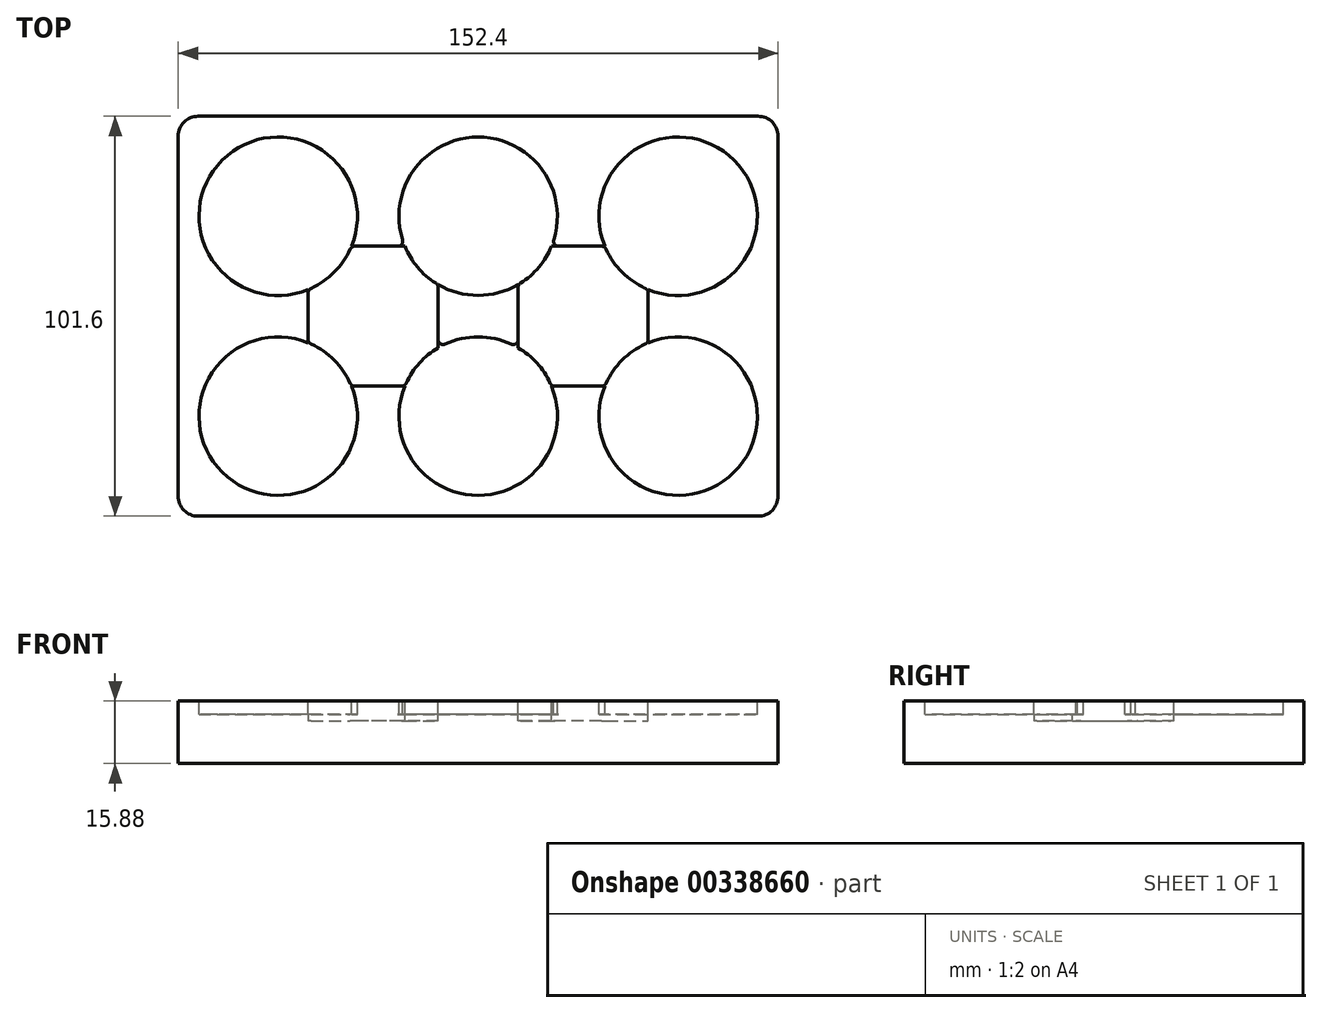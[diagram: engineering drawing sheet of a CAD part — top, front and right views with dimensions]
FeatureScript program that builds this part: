
annotation { "Feature Type Name" : "Feature", "Feature Type Description" : "" }
export const myFeature = defineFeature(function(context is Context, id is Id, definition is map)
    precondition{}
    {
        {
            var Q0;
            Q0=qCreatedBy(makeId("Top.planeOp"),FACE);
            var sketch = newSketch(context, id + "F0", { "sketchPlane" : qUnion([Q0])});
            skLineSegment(sketch, "E0.bottom", {"start": v(0, 0) * mm, "end": v(33.02, 0) * mm});
            skLineSegment(sketch, "E0.top", {"start": v(0, 101.6) * mm, "end": v(25.4, 101.6) * mm});
            skLineSegment(sketch, "E0.left", {"start": v(0, 0) * mm, "end": v(0, 25.4) * mm});
            skLineSegment(sketch, "E0.right", {"start": v(152.4, 0) * mm, "end": v(152.4, 33.02) * mm});
            skCircle(sketch, "E1", {"center": v(25.4, 25.4) * mm, "radius": 20.13 * mm});
            skCircle(sketch, "E2", {"center": v(25.4, 76.2) * mm, "radius": 20.13 * mm});
            skLineSegment(sketch, "E3", {"start": v(0, 76.2) * mm, "end": v(0, 101.6) * mm});
            skLineSegment(sketch, "E4", {"start": v(0, 25.4) * mm, "end": v(0, 76.2) * mm});
            skLineSegment(sketch, "E5", {"start": v(25.4, 101.6) * mm, "end": v(76.2, 101.6) * mm});
            skLineSegment(sketch, "E6", {"start": v(76.2, 101.6) * mm, "end": v(127, 101.6) * mm});
            skLineSegment(sketch, "E7", {"start": v(127, 101.6) * mm, "end": v(152.4, 101.6) * mm});
            skCircle(sketch, "E8", {"center": v(76.2, 76.2) * mm, "radius": 20.13 * mm});
            skCircle(sketch, "E9", {"center": v(76.2, 25.4) * mm, "radius": 20.13 * mm});
            skCircle(sketch, "E10", {"center": v(127, 76.2) * mm, "radius": 20.13 * mm});
            skCircle(sketch, "E11", {"center": v(127, 25.4) * mm, "radius": 20.13 * mm});
            skLineSegment(sketch, "E12", {"start": v(33.02, 0) * mm, "end": v(66.04, 0) * mm});
            skLineSegment(sketch, "E13", {"start": v(66.04, 0) * mm, "end": v(76.2, 0) * mm});
            skLineSegment(sketch, "E14", {"start": v(86.36, 0) * mm, "end": v(119.38, 0) * mm});
            skLineSegment(sketch, "E15", {"start": v(119.38, 0) * mm, "end": v(152.4, 0) * mm});
            skLineSegment(sketch, "E16", {"start": v(152.4, 33.02) * mm, "end": v(152.4, 68.58) * mm});
            skLineSegment(sketch, "E17", {"start": v(152.4, 68.58) * mm, "end": v(152.4, 101.6) * mm});
            skLineSegment(sketch, "E18", {"start": v(76.2, 0) * mm, "end": v(86.36, 0) * mm});
            skLineSegment(sketch, "E19.trimOffspring", {"start": v(57.57, 68.58) * mm, "end": v(44.03, 68.58) * mm});
            skLineSegment(sketch, "E20.trimOffspring", {"start": v(108.37, 68.58) * mm, "end": v(94.83, 68.58) * mm});
            skLineSegment(sketch, "E21.trimOffspring", {"start": v(119.38, 44.03) * mm, "end": v(119.38, 57.57) * mm});
            skLineSegment(sketch, "E22.trimOffspring", {"start": v(108.37, 33.02) * mm, "end": v(94.83, 33.02) * mm});
            skLineSegment(sketch, "E23.trimOffspring", {"start": v(57.57, 33.02) * mm, "end": v(44.03, 33.02) * mm});
            skLineSegment(sketch, "E24.trimOffspring", {"start": v(66.04, 42.78) * mm, "end": v(66.04, 58.82) * mm});
            skLineSegment(sketch, "E25.trimOffspring", {"start": v(33.02, 44.03) * mm, "end": v(33.02, 57.57) * mm});
            skLineSegment(sketch, "E26.trimOffspring", {"start": v(86.36, 42.78) * mm, "end": v(86.36, 58.82) * mm});
            skSolve(sketch);
        }
        {
            var Q0;
            {var subQ0=sQuery(id+"F0.wireOp",EDGE,"E19.trimOffspring");Q0=makeQuery(id+"F0.imprint","IMPRINT",FACE,{"disambiguationData":[TD([[makeQuery(id+"F0.imprint","IMPRINT",EDGE,{"derivedFrom":subQ0}),1.0]])]});}
            var Q1;
            {var subQ0=sQuery(id+"F0.wireOp",EDGE,"E2");var subQ1=makeQuery(id+"F0.imprint","INTERSECT",VERTEX,{"derivedFrom":[subQ0,sQuery(id+"F0.wireOp",EDGE,"E19.trimOffspring")]});Q1=makeQuery(id+"F0.imprint","IMPRINT",FACE,{"disambiguationData":[TD([[makeQuery(id+"F0.imprint","IMPRINT",EDGE,{"disambiguationData":[TD([[subQ1,1.0]])],"derivedFrom":subQ0}),1.0]])]});}
            var Q2;
            {var subQ0=sQuery(id+"F0.wireOp",EDGE,"E1");var subQ1=makeQuery(id+"F0.imprint","INTERSECT",VERTEX,{"derivedFrom":[subQ0,sQuery(id+"F0.wireOp",EDGE,"E23.trimOffspring")]});Q2=makeQuery(id+"F0.imprint","IMPRINT",FACE,{"disambiguationData":[TD([[makeQuery(id+"F0.imprint","IMPRINT",EDGE,{"disambiguationData":[TD([[subQ1,-1.0]])],"derivedFrom":subQ0}),1.0]])]});}
            var Q3;
            {var subQ0=sQuery(id+"F0.wireOp",EDGE,"E9");var subQ1=makeQuery(id+"F0.imprint","INTERSECT",VERTEX,{"derivedFrom":[subQ0,sQuery(id+"F0.wireOp",EDGE,"E22.trimOffspring")]});Q3=makeQuery(id+"F0.imprint","IMPRINT",FACE,{"disambiguationData":[TD([[makeQuery(id+"F0.imprint","IMPRINT",EDGE,{"disambiguationData":[TD([[subQ1,-1.0]])],"derivedFrom":subQ0}),1.0]])]});}
            var Q4;
            {var subQ0=sQuery(id+"F0.wireOp",EDGE,"E10");var subQ1=makeQuery(id+"F0.imprint","INTERSECT",VERTEX,{"derivedFrom":[subQ0,sQuery(id+"F0.wireOp",EDGE,"E20.trimOffspring")]});Q4=makeQuery(id+"F0.imprint","IMPRINT",FACE,{"disambiguationData":[TD([[makeQuery(id+"F0.imprint","IMPRINT",EDGE,{"disambiguationData":[TD([[subQ1,-1.0]])],"derivedFrom":subQ0}),1.0]])]});}
            var Q5;
            {var subQ0=sQuery(id+"F0.wireOp",EDGE,"E24.trimOffspring");Q5=makeQuery(id+"F0.imprint","IMPRINT",FACE,{"disambiguationData":[TD([[makeQuery(id+"F0.imprint","IMPRINT",EDGE,{"derivedFrom":subQ0}),-1.0]])]});}
            var Q6;
            {var subQ3=sQuery(id+"F0.wireOp",EDGE,"E20.trimOffspring");Q6=makeQuery(id+"F0.imprint","IMPRINT",FACE,{"disambiguationData":[TD([[makeQuery(id+"F0.imprint","IMPRINT",EDGE,{"derivedFrom":subQ3}),1.0]])]});}
            var Q7;
            {var subQ0=sQuery(id+"F0.wireOp",EDGE,"E8");var subQ1=makeQuery(id+"F0.imprint","INTERSECT",VERTEX,{"derivedFrom":[subQ0,sQuery(id+"F0.wireOp",EDGE,"E19.trimOffspring")]});Q7=makeQuery(id+"F0.imprint","IMPRINT",FACE,{"disambiguationData":[TD([[makeQuery(id+"F0.imprint","IMPRINT",EDGE,{"disambiguationData":[TD([[subQ1,-1.0]])],"derivedFrom":subQ0}),1.0]])]});}
            var Q8;
            {var subQ0=sQuery(id+"F0.wireOp",EDGE,"E11");var subQ1=makeQuery(id+"F0.imprint","INTERSECT",VERTEX,{"derivedFrom":[subQ0,sQuery(id+"F0.wireOp",EDGE,"E21.trimOffspring")]});Q8=makeQuery(id+"F0.imprint","IMPRINT",FACE,{"disambiguationData":[TD([[makeQuery(id+"F0.imprint","IMPRINT",EDGE,{"disambiguationData":[TD([[subQ1,-1.0]])],"derivedFrom":subQ0}),1.0]])]});}
            var Q9;
            Q9=makeQuery(id+"F0.imprint","IMPRINT",FACE,{"disambiguationData":[TD([[makeQuery(id+"F0.imprint","IMPRINT",EDGE,{"derivedFrom":sQuery(id+"F0.wireOp",EDGE,"E0.bottom")}),1.0]])]});
            extrude(context, id + "F1", {"entities" : qUnion([Q0, Q1, Q2, Q3, Q4, Q5, Q6, Q7, Q8, Q9]), "oppositeDirection" : true, "depth" : 15.88 * mm});
        }
        {
            var Q0;
            {var subQ0=sQuery(id+"F0.wireOp",EDGE,"E2");var subQ1=makeQuery(id+"F0.imprint","INTERSECT",VERTEX,{"derivedFrom":[subQ0,sQuery(id+"F0.wireOp",EDGE,"E19.trimOffspring")]});Q0=makeQuery(id+"F0.imprint","IMPRINT",FACE,{"disambiguationData":[TD([[makeQuery(id+"F0.imprint","IMPRINT",EDGE,{"disambiguationData":[TD([[subQ1,1.0]])],"derivedFrom":subQ0}),1.0]])]});}
            var Q1;
            {var subQ0=sQuery(id+"F0.wireOp",EDGE,"E1");var subQ1=makeQuery(id+"F0.imprint","INTERSECT",VERTEX,{"derivedFrom":[subQ0,sQuery(id+"F0.wireOp",EDGE,"E23.trimOffspring")]});Q1=makeQuery(id+"F0.imprint","IMPRINT",FACE,{"disambiguationData":[TD([[makeQuery(id+"F0.imprint","IMPRINT",EDGE,{"disambiguationData":[TD([[subQ1,-1.0]])],"derivedFrom":subQ0}),1.0]])]});}
            var Q2;
            {var subQ0=sQuery(id+"F0.wireOp",EDGE,"E9");var subQ1=makeQuery(id+"F0.imprint","INTERSECT",VERTEX,{"derivedFrom":[subQ0,sQuery(id+"F0.wireOp",EDGE,"E22.trimOffspring")]});Q2=makeQuery(id+"F0.imprint","IMPRINT",FACE,{"disambiguationData":[TD([[makeQuery(id+"F0.imprint","IMPRINT",EDGE,{"disambiguationData":[TD([[subQ1,-1.0]])],"derivedFrom":subQ0}),1.0]])]});}
            var Q3;
            {var subQ0=sQuery(id+"F0.wireOp",EDGE,"E8");var subQ1=makeQuery(id+"F0.imprint","INTERSECT",VERTEX,{"derivedFrom":[subQ0,sQuery(id+"F0.wireOp",EDGE,"E19.trimOffspring")]});Q3=makeQuery(id+"F0.imprint","IMPRINT",FACE,{"disambiguationData":[TD([[makeQuery(id+"F0.imprint","IMPRINT",EDGE,{"disambiguationData":[TD([[subQ1,-1.0]])],"derivedFrom":subQ0}),1.0]])]});}
            var Q4;
            {var subQ0=sQuery(id+"F0.wireOp",EDGE,"E10");var subQ1=makeQuery(id+"F0.imprint","INTERSECT",VERTEX,{"derivedFrom":[subQ0,sQuery(id+"F0.wireOp",EDGE,"E20.trimOffspring")]});Q4=makeQuery(id+"F0.imprint","IMPRINT",FACE,{"disambiguationData":[TD([[makeQuery(id+"F0.imprint","IMPRINT",EDGE,{"disambiguationData":[TD([[subQ1,-1.0]])],"derivedFrom":subQ0}),1.0]])]});}
            var Q5;
            {var subQ0=sQuery(id+"F0.wireOp",EDGE,"E11");var subQ1=makeQuery(id+"F0.imprint","INTERSECT",VERTEX,{"derivedFrom":[subQ0,sQuery(id+"F0.wireOp",EDGE,"E21.trimOffspring")]});Q5=makeQuery(id+"F0.imprint","IMPRINT",FACE,{"disambiguationData":[TD([[makeQuery(id+"F0.imprint","IMPRINT",EDGE,{"disambiguationData":[TD([[subQ1,-1.0]])],"derivedFrom":subQ0}),1.0]])]});}
            extrude(context, id + "F2", {"entities" : qUnion([Q0, Q1, Q2, Q3, Q4, Q5]), "operationType" : NewBodyOperationType.REMOVE, "oppositeDirection" : true, "depth" : 3.35 * mm});
        }
        {
            var Q0;
            {var subQ0=sQuery(id+"F0.wireOp",EDGE,"E19.trimOffspring");Q0=makeQuery(id+"F0.imprint","IMPRINT",FACE,{"disambiguationData":[TD([[makeQuery(id+"F0.imprint","IMPRINT",EDGE,{"derivedFrom":subQ0}),1.0]])]});}
            var Q1;
            {var subQ3=sQuery(id+"F0.wireOp",EDGE,"E20.trimOffspring");Q1=makeQuery(id+"F0.imprint","IMPRINT",FACE,{"disambiguationData":[TD([[makeQuery(id+"F0.imprint","IMPRINT",EDGE,{"derivedFrom":subQ3}),1.0]])]});}
            extrude(context, id + "F3", {"entities" : qUnion([Q0, Q1]), "operationType" : NewBodyOperationType.REMOVE, "oppositeDirection" : true, "depth" : 5.08 * mm});
        }
        {
            var Q0;
            Q0=makeQuery(id+"F1.opExtrude","SWEPT_EDGE",EDGE,{"disambiguationData":[OSD([sQuery(id+"F0.wireOp",EDGE,"E0.bottom"),sQuery(id+"F0.wireOp",EDGE,"E0.left")])]});
            var Q1;
            Q1=makeQuery(id+"F1.opExtrude","SWEPT_EDGE",EDGE,{"disambiguationData":[OSD([sQuery(id+"F0.wireOp",EDGE,"E0.right"),sQuery(id+"F0.wireOp",EDGE,"E15")])]});
            var Q2;
            Q2=makeQuery(id+"F1.opExtrude","SWEPT_EDGE",EDGE,{"disambiguationData":[OSD([sQuery(id+"F0.wireOp",EDGE,"E7"),sQuery(id+"F0.wireOp",EDGE,"E17")])]});
            var Q3;
            Q3=makeQuery(id+"F1.opExtrude","SWEPT_EDGE",EDGE,{"disambiguationData":[OSD([sQuery(id+"F0.wireOp",EDGE,"E0.top"),sQuery(id+"F0.wireOp",EDGE,"E3")])]});
            fillet(context, id + "F4", {"entities" : qUnion([Q0, Q1, Q2, Q3]), "radius" : 5.08 * mm, "tangentPropagation" : true, "allowEdgeOverflow" : false});
        }
        {
            var Q0;
            {var subQ0=sQuery(id+"F0.wireOp",EDGE,"E8");var subQ1=sQuery(id+"F0.wireOp",EDGE,"E26.trimOffspring");Q0=makeQuery(id+"F3.boolean.opBoolean","COPY",EDGE,{"disambiguationData":[topologyDisambiguationEdgeConnected([makeQuery(id+"F2.boolean.opBoolean","COPY",FACE,{"derivedFrom":makeQuery(id+"F2.opExtrude","SWEPT_FACE",FACE,{"disambiguationData":[OSD([subQ0])]})})])],"derivedFrom":makeQuery(id+"F3.opExtrude","SWEPT_EDGE",EDGE,{"disambiguationData":[OSD([subQ0,subQ1])]})});}
            var Q1;
            {var subQ0=sQuery(id+"F0.wireOp",EDGE,"E8");var subQ1=sQuery(id+"F0.wireOp",EDGE,"E20.trimOffspring");Q1=makeQuery(id+"F3.boolean.opBoolean","COPY",EDGE,{"disambiguationData":[topologyDisambiguationEdgeConnected([makeQuery(id+"F2.boolean.opBoolean","COPY",FACE,{"derivedFrom":makeQuery(id+"F2.opExtrude","SWEPT_FACE",FACE,{"disambiguationData":[OSD([subQ0])]})})])],"derivedFrom":makeQuery(id+"F3.opExtrude","SWEPT_EDGE",EDGE,{"disambiguationData":[OSD([subQ0,subQ1])]})});}
            var Q2;
            {var subQ0=sQuery(id+"F0.wireOp",EDGE,"E10");var subQ1=sQuery(id+"F0.wireOp",EDGE,"E20.trimOffspring");Q2=makeQuery(id+"F3.boolean.opBoolean","COPY",EDGE,{"disambiguationData":[topologyDisambiguationEdgeConnected([makeQuery(id+"F2.boolean.opBoolean","COPY",FACE,{"derivedFrom":makeQuery(id+"F2.opExtrude","SWEPT_FACE",FACE,{"disambiguationData":[OSD([subQ0])]})})])],"derivedFrom":makeQuery(id+"F3.opExtrude","SWEPT_EDGE",EDGE,{"disambiguationData":[OSD([subQ0,subQ1])]})});}
            var Q3;
            {var subQ0=sQuery(id+"F0.wireOp",EDGE,"E10");var subQ1=sQuery(id+"F0.wireOp",EDGE,"E21.trimOffspring");Q3=makeQuery(id+"F3.boolean.opBoolean","COPY",EDGE,{"disambiguationData":[topologyDisambiguationEdgeConnected([makeQuery(id+"F2.boolean.opBoolean","COPY",FACE,{"derivedFrom":makeQuery(id+"F2.opExtrude","SWEPT_FACE",FACE,{"disambiguationData":[OSD([subQ0])]})})])],"derivedFrom":makeQuery(id+"F3.opExtrude","SWEPT_EDGE",EDGE,{"disambiguationData":[OSD([subQ0,subQ1])]})});}
            var Q4;
            {var subQ0=sQuery(id+"F0.wireOp",EDGE,"E11");var subQ1=sQuery(id+"F0.wireOp",EDGE,"E21.trimOffspring");Q4=makeQuery(id+"F3.boolean.opBoolean","COPY",EDGE,{"disambiguationData":[topologyDisambiguationEdgeConnected([makeQuery(id+"F2.boolean.opBoolean","COPY",FACE,{"derivedFrom":makeQuery(id+"F2.opExtrude","SWEPT_FACE",FACE,{"disambiguationData":[OSD([subQ0])]})})])],"derivedFrom":makeQuery(id+"F3.opExtrude","SWEPT_EDGE",EDGE,{"disambiguationData":[OSD([subQ0,subQ1])]})});}
            var Q5;
            {var subQ0=sQuery(id+"F0.wireOp",EDGE,"E11");var subQ1=sQuery(id+"F0.wireOp",EDGE,"E22.trimOffspring");Q5=makeQuery(id+"F3.boolean.opBoolean","COPY",EDGE,{"disambiguationData":[topologyDisambiguationEdgeConnected([makeQuery(id+"F2.boolean.opBoolean","COPY",FACE,{"derivedFrom":makeQuery(id+"F2.opExtrude","SWEPT_FACE",FACE,{"disambiguationData":[OSD([subQ0])]})})])],"derivedFrom":makeQuery(id+"F3.opExtrude","SWEPT_EDGE",EDGE,{"disambiguationData":[OSD([subQ0,subQ1])]})});}
            var Q6;
            {var subQ0=sQuery(id+"F0.wireOp",EDGE,"E9");var subQ1=sQuery(id+"F0.wireOp",EDGE,"E22.trimOffspring");Q6=makeQuery(id+"F3.boolean.opBoolean","COPY",EDGE,{"disambiguationData":[topologyDisambiguationEdgeConnected([makeQuery(id+"F2.boolean.opBoolean","COPY",FACE,{"derivedFrom":makeQuery(id+"F2.opExtrude","SWEPT_FACE",FACE,{"disambiguationData":[OSD([subQ0])]})})])],"derivedFrom":makeQuery(id+"F3.opExtrude","SWEPT_EDGE",EDGE,{"disambiguationData":[OSD([subQ0,subQ1])]})});}
            var Q7;
            {var subQ0=sQuery(id+"F0.wireOp",EDGE,"E9");var subQ1=sQuery(id+"F0.wireOp",EDGE,"E26.trimOffspring");Q7=makeQuery(id+"F3.boolean.opBoolean","COPY",EDGE,{"disambiguationData":[topologyDisambiguationEdgeConnected([makeQuery(id+"F2.boolean.opBoolean","COPY",FACE,{"derivedFrom":makeQuery(id+"F2.opExtrude","SWEPT_FACE",FACE,{"disambiguationData":[OSD([subQ0])]})})])],"derivedFrom":makeQuery(id+"F3.opExtrude","SWEPT_EDGE",EDGE,{"disambiguationData":[OSD([subQ0,subQ1])]})});}
            var Q8;
            {var subQ0=sQuery(id+"F0.wireOp",EDGE,"E9");var subQ1=sQuery(id+"F0.wireOp",EDGE,"E24.trimOffspring");Q8=makeQuery(id+"F3.boolean.opBoolean","COPY",EDGE,{"disambiguationData":[topologyDisambiguationEdgeConnected([makeQuery(id+"F2.boolean.opBoolean","COPY",FACE,{"derivedFrom":makeQuery(id+"F2.opExtrude","SWEPT_FACE",FACE,{"disambiguationData":[OSD([subQ0])]})})])],"derivedFrom":makeQuery(id+"F3.opExtrude","SWEPT_EDGE",EDGE,{"disambiguationData":[OSD([subQ0,subQ1])]})});}
            var Q9;
            {var subQ0=sQuery(id+"F0.wireOp",EDGE,"E9");var subQ1=sQuery(id+"F0.wireOp",EDGE,"E23.trimOffspring");Q9=makeQuery(id+"F3.boolean.opBoolean","COPY",EDGE,{"disambiguationData":[topologyDisambiguationEdgeConnected([makeQuery(id+"F2.boolean.opBoolean","COPY",FACE,{"derivedFrom":makeQuery(id+"F2.opExtrude","SWEPT_FACE",FACE,{"disambiguationData":[OSD([subQ0])]})})])],"derivedFrom":makeQuery(id+"F3.opExtrude","SWEPT_EDGE",EDGE,{"disambiguationData":[OSD([subQ0,subQ1])]})});}
            var Q10;
            {var subQ0=sQuery(id+"F0.wireOp",EDGE,"E1");var subQ1=sQuery(id+"F0.wireOp",EDGE,"E23.trimOffspring");Q10=makeQuery(id+"F3.boolean.opBoolean","COPY",EDGE,{"disambiguationData":[topologyDisambiguationEdgeConnected([makeQuery(id+"F2.boolean.opBoolean","COPY",FACE,{"derivedFrom":makeQuery(id+"F2.opExtrude","SWEPT_FACE",FACE,{"disambiguationData":[OSD([subQ0])]})})])],"derivedFrom":makeQuery(id+"F3.opExtrude","SWEPT_EDGE",EDGE,{"disambiguationData":[OSD([subQ0,subQ1])]})});}
            var Q11;
            {var subQ0=sQuery(id+"F0.wireOp",EDGE,"E1");var subQ1=sQuery(id+"F0.wireOp",EDGE,"E25.trimOffspring");Q11=makeQuery(id+"F3.boolean.opBoolean","COPY",EDGE,{"disambiguationData":[topologyDisambiguationEdgeConnected([makeQuery(id+"F2.boolean.opBoolean","COPY",FACE,{"derivedFrom":makeQuery(id+"F2.opExtrude","SWEPT_FACE",FACE,{"disambiguationData":[OSD([subQ0])]})})])],"derivedFrom":makeQuery(id+"F3.opExtrude","SWEPT_EDGE",EDGE,{"disambiguationData":[OSD([subQ0,subQ1])]})});}
            var Q12;
            {var subQ0=sQuery(id+"F0.wireOp",EDGE,"E2");var subQ1=sQuery(id+"F0.wireOp",EDGE,"E25.trimOffspring");Q12=makeQuery(id+"F3.boolean.opBoolean","COPY",EDGE,{"disambiguationData":[topologyDisambiguationEdgeConnected([makeQuery(id+"F2.boolean.opBoolean","COPY",FACE,{"derivedFrom":makeQuery(id+"F2.opExtrude","SWEPT_FACE",FACE,{"disambiguationData":[OSD([subQ0])]})})])],"derivedFrom":makeQuery(id+"F3.opExtrude","SWEPT_EDGE",EDGE,{"disambiguationData":[OSD([subQ0,subQ1])]})});}
            var Q13;
            {var subQ0=sQuery(id+"F0.wireOp",EDGE,"E2");var subQ1=sQuery(id+"F0.wireOp",EDGE,"E19.trimOffspring");Q13=makeQuery(id+"F3.boolean.opBoolean","COPY",EDGE,{"disambiguationData":[topologyDisambiguationEdgeConnected([makeQuery(id+"F2.boolean.opBoolean","COPY",FACE,{"derivedFrom":makeQuery(id+"F2.opExtrude","SWEPT_FACE",FACE,{"disambiguationData":[OSD([subQ0])]})})])],"derivedFrom":makeQuery(id+"F3.opExtrude","SWEPT_EDGE",EDGE,{"disambiguationData":[OSD([subQ0,subQ1])]})});}
            var Q14;
            {var subQ0=sQuery(id+"F0.wireOp",EDGE,"E8");var subQ1=sQuery(id+"F0.wireOp",EDGE,"E19.trimOffspring");Q14=makeQuery(id+"F3.boolean.opBoolean","COPY",EDGE,{"disambiguationData":[topologyDisambiguationEdgeConnected([makeQuery(id+"F2.boolean.opBoolean","COPY",FACE,{"derivedFrom":makeQuery(id+"F2.opExtrude","SWEPT_FACE",FACE,{"disambiguationData":[OSD([subQ0])]})})])],"derivedFrom":makeQuery(id+"F3.opExtrude","SWEPT_EDGE",EDGE,{"disambiguationData":[OSD([subQ0,subQ1])]})});}
            var Q15;
            {var subQ0=sQuery(id+"F0.wireOp",EDGE,"E8");var subQ1=sQuery(id+"F0.wireOp",EDGE,"E24.trimOffspring");Q15=makeQuery(id+"F3.boolean.opBoolean","COPY",EDGE,{"disambiguationData":[topologyDisambiguationEdgeConnected([makeQuery(id+"F2.boolean.opBoolean","COPY",FACE,{"derivedFrom":makeQuery(id+"F2.opExtrude","SWEPT_FACE",FACE,{"disambiguationData":[OSD([subQ0])]})})])],"derivedFrom":makeQuery(id+"F3.opExtrude","SWEPT_EDGE",EDGE,{"disambiguationData":[OSD([subQ0,subQ1])]})});}
            fillet(context, id + "F5", {"entities" : qUnion([Q0, Q1, Q2, Q3, Q4, Q5, Q6, Q7, Q8, Q9, Q10, Q11, Q12, Q13, Q14, Q15]), "radius" : 1.27 * mm, "tangentPropagation" : true, "allowEdgeOverflow" : false});
        }
    });
